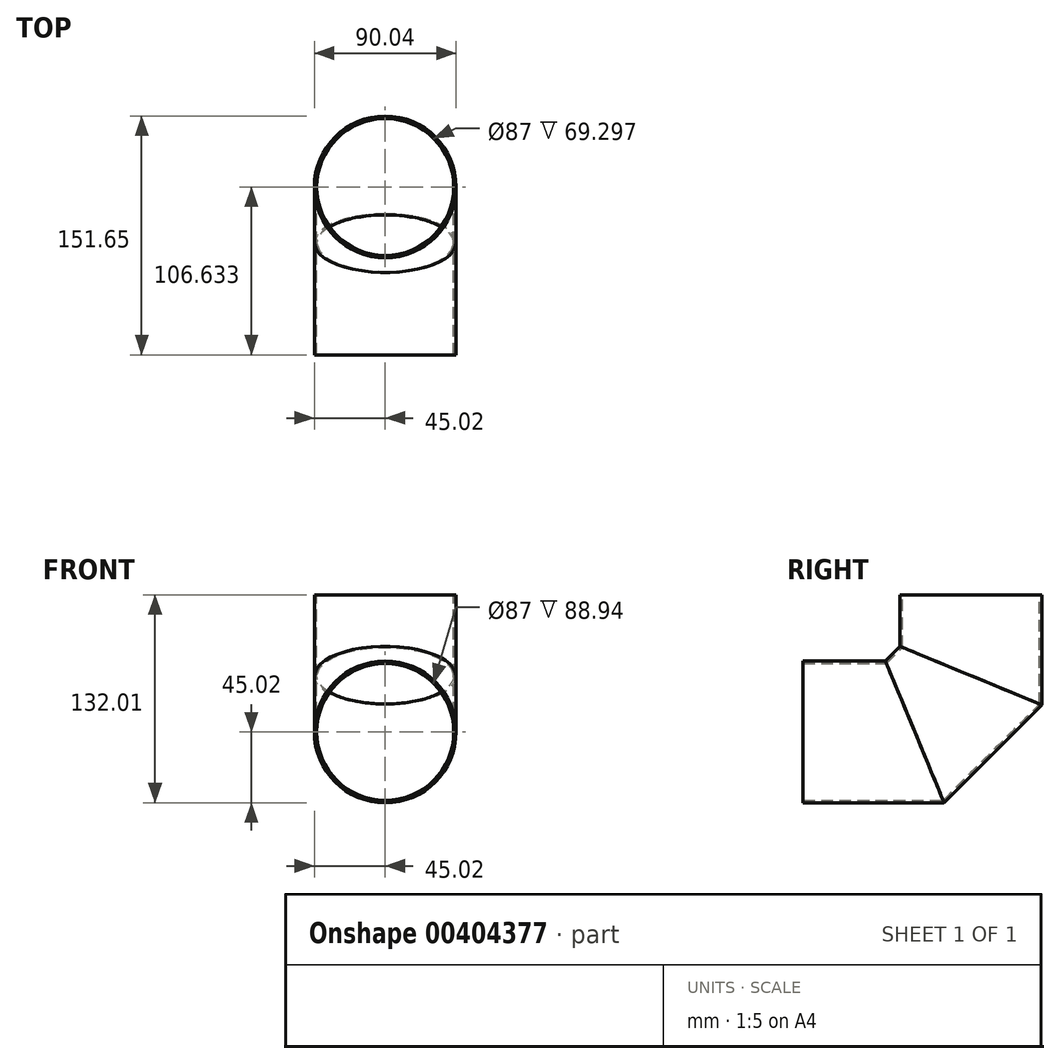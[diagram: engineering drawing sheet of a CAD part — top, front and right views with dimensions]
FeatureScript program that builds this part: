
annotation { "Feature Type Name" : "Feature", "Feature Type Description" : "" }
export const myFeature = defineFeature(function(context is Context, id is Id, definition is map)
    precondition{}
    {
        {
            var Q0;
            Q0=qCreatedBy(makeId("Front.planeOp"),FACE);
            cPlane(context, id + "F0", {"entities" : qUnion([Q0]), "cplaneType" : CPlaneType.OFFSET, "offset" : 70 * mm, "width" : 150 * mm, "height" : 150 * mm});
        }
        {
            var Q0;
            Q0=qCreatedBy(id+"F0.planeOp",FACE);
            var sketch = newSketch(context, id + "F1", { "sketchPlane" : qUnion([Q0])});
            skCircle(sketch, "E0", {"center": v(0, 0) * mm, "radius": 45.02 * mm});
            skCircle(sketch, "E1", {"center": v(0, 0) * mm, "radius": 43.5 * mm});
            skSolve(sketch);
        }
        {
            var Q0;
            Q0=qCreatedBy(makeId("Right.planeOp"),FACE);
            var sketch = newSketch(context, id + "F2", { "sketchPlane" : qUnion([Q0])});
            skLineSegment(sketch, "E2", {"start": v(-69.9, 0) * mm, "end": v(0.91, 0) * mm});
            skLineSegment(sketch, "E3", {"start": v(140.02, 156.24) * mm, "end": v(140.02, 156.63) * mm});
            skLineSegment(sketch, "E4", {"start": v(0.91, 0) * mm, "end": v(36.63, 35.72) * mm});
            skLineSegment(sketch, "E5", {"start": v(36.63, 35.72) * mm, "end": v(36.63, 87.1) * mm});
            skLineSegment(sketch, "E6", {"start": v(36.63, 84.15) * mm, "end": v(36.63, -52.2) * mm, "construction": true});
            skSolve(sketch);
        }
        {
            var Q0;
            Q0=makeQuery(id+"F1.imprint","IMPRINT",FACE,{"disambiguationData":[TD([[makeQuery(id+"F1.imprint","IMPRINT",EDGE,{"derivedFrom":sQuery(id+"F1.wireOp",EDGE,"E0")}),1.0]])]});
            var Q1;
            Q1=sQuery(id+"F2.wireOp",EDGE,"E2");
            var Q2;
            Q2=sQuery(id+"F2.wireOp",EDGE,"nZaEgCqf-vknP-4DVJ-eaiq-E1KxRphXymNN");
            var Q3;
            Q3=sQuery(id+"F2.wireOp",EDGE,"E4");
            var Q4;
            Q4=sQuery(id+"F2.wireOp",EDGE,"E5");
            sweep(context, id + "F3", {"profiles" : qUnion([Q0]), "path" : qUnion([Q1, Q2, Q3, Q4])});
        }
    });
